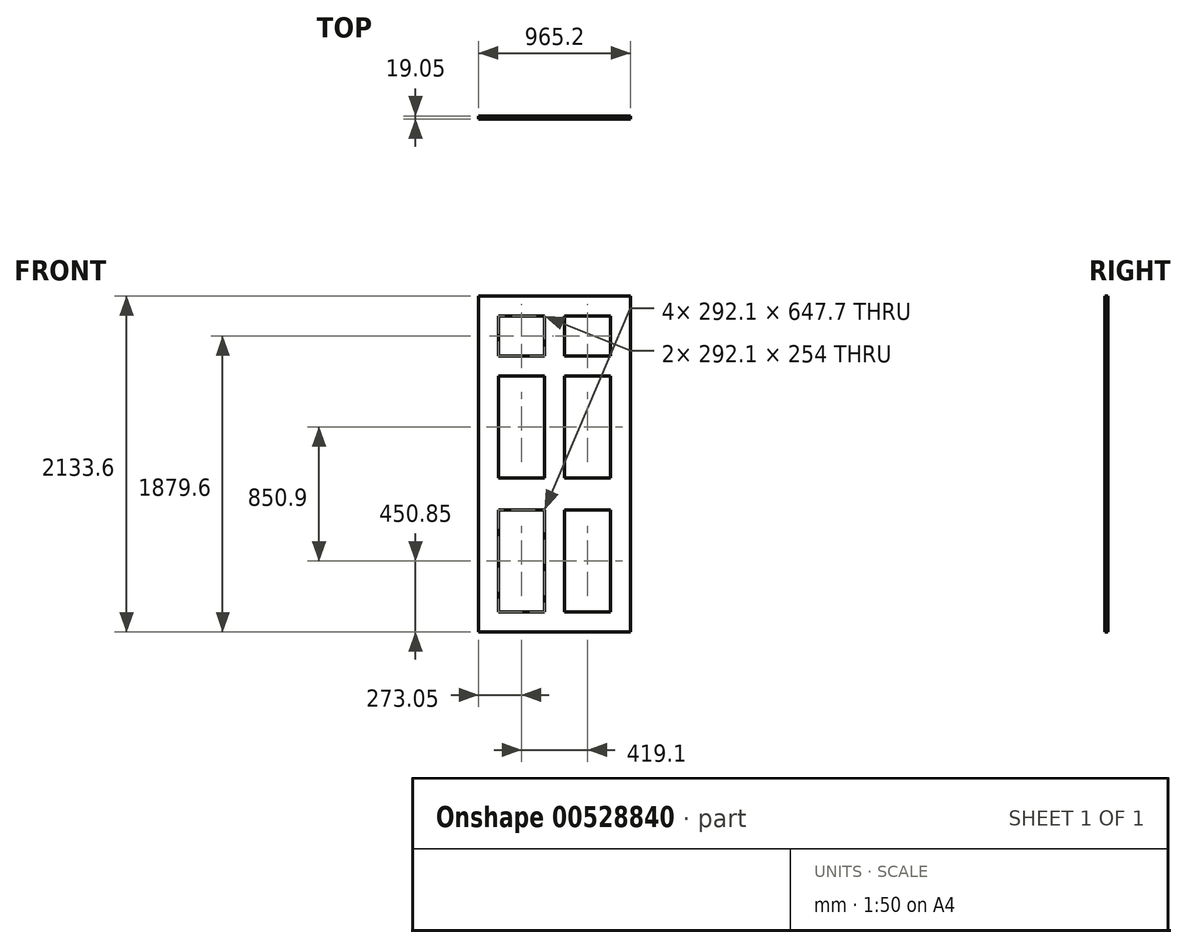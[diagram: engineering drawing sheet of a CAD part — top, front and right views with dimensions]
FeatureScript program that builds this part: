
annotation { "Feature Type Name" : "Feature", "Feature Type Description" : "" }
export const myFeature = defineFeature(function(context is Context, id is Id, definition is map)
    precondition{}
    {
        {
            var Q0;
            Q0=qCreatedBy(makeId("Front.planeOp"),FACE);
            var sketch = newSketch(context, id + "F0", { "sketchPlane" : qUnion([Q0])});
            skLineSegment(sketch, "E0.bottom", {"start": v(482.6, -1066.8) * mm, "end": v(-482.6, -1066.8) * mm});
            skLineSegment(sketch, "E0.top", {"start": v(482.6, 1066.8) * mm, "end": v(-482.6, 1066.8) * mm});
            skLineSegment(sketch, "E0.left", {"start": v(482.6, -1066.8) * mm, "end": v(482.6, 1066.8) * mm});
            skLineSegment(sketch, "E0.right", {"start": v(-482.6, -1066.8) * mm, "end": v(-482.6, 1066.8) * mm});
            skPoint(sketch, "E0.middle", {"position": v(0, 0) * mm});
            skLineSegment(sketch, "E1", {"start": v(-355.6, 939.8) * mm, "end": v(-355.6, -88.9) * mm});
            skLineSegment(sketch, "E2", {"start": v(-355.6, 939.8) * mm, "end": v(-63.5, 939.8) * mm});
            skPoint(sketch, "E3.orphan", {"position": v(-355.6, 1066.8) * mm});
            skLineSegment(sketch, "E4", {"start": v(355.6, 939.8) * mm, "end": v(355.6, 685.8) * mm});
            skPoint(sketch, "E5.orphan", {"position": v(482.6, 939.8) * mm});
            skLineSegment(sketch, "E6", {"start": v(-355.6, -939.8) * mm, "end": v(-63.5, -939.8) * mm});
            skPoint(sketch, "E7.orphan", {"position": v(-355.6, -1066.8) * mm});
            skPoint(sketch, "E8.orphan", {"position": v(355.6, -1066.8) * mm});
            skPoint(sketch, "E9.orphan", {"position": v(-482.6, -939.8) * mm});
            skLineSegment(sketch, "E10", {"start": v(-63.5, 939.8) * mm, "end": v(-63.5, 685.8) * mm});
            skLineSegment(sketch, "E11", {"start": v(63.5, -939.8) * mm, "end": v(63.5, -292.1) * mm});
            skLineSegment(sketch, "E12", {"start": v(-355.6, 685.8) * mm, "end": v(-63.5, 685.8) * mm});
            skLineSegment(sketch, "E13.trimOffspring", {"start": v(63.5, 939.8) * mm, "end": v(355.6, 939.8) * mm});
            skLineSegment(sketch, "E14.trimOffspring", {"start": v(63.5, 685.8) * mm, "end": v(355.6, 685.8) * mm});
            skLineSegment(sketch, "E15", {"start": v(-355.6, 558.8) * mm, "end": v(-63.5, 558.8) * mm});
            skLineSegment(sketch, "E16.trimOffspring", {"start": v(-63.5, 558.8) * mm, "end": v(-63.5, -88.9) * mm});
            skLineSegment(sketch, "E17.trimOffspring", {"start": v(63.5, 685.8) * mm, "end": v(63.5, 939.8) * mm});
            skLineSegment(sketch, "E18.trimOffspring", {"start": v(355.6, 558.8) * mm, "end": v(355.6, -88.9) * mm});
            skLineSegment(sketch, "E19.trimOffspring", {"start": v(63.5, 558.8) * mm, "end": v(355.6, 558.8) * mm});
            skLineSegment(sketch, "E20", {"start": v(-355.6, -88.9) * mm, "end": v(-63.5, -88.9) * mm});
            skLineSegment(sketch, "E21", {"start": v(-355.6, -292.1) * mm, "end": v(-63.5, -292.1) * mm});
            skLineSegment(sketch, "E22.trimOffspring", {"start": v(-63.5, -292.1) * mm, "end": v(-63.5, -939.8) * mm});
            skLineSegment(sketch, "E23.trimOffspring", {"start": v(63.5, -88.9) * mm, "end": v(355.6, -88.9) * mm});
            skLineSegment(sketch, "E24.trimOffspring", {"start": v(355.6, -292.1) * mm, "end": v(355.6, -939.8) * mm});
            skLineSegment(sketch, "E25.trimOffspring", {"start": v(63.5, -88.9) * mm, "end": v(63.5, 558.8) * mm});
            skLineSegment(sketch, "E26.trimOffspring", {"start": v(-355.6, -292.1) * mm, "end": v(-355.6, -939.8) * mm});
            skLineSegment(sketch, "E27.trimOffspring", {"start": v(63.5, -292.1) * mm, "end": v(355.6, -292.1) * mm});
            skLineSegment(sketch, "E28.trimOffspring", {"start": v(63.5, -939.8) * mm, "end": v(355.6, -939.8) * mm});
            skSolve(sketch);
        }
        {
            var Q0;
            Q0=qSketchRegion(id+"F0",true);
            extrude(context, id + "F1", {"entities" : qUnion([Q0]), "depth" : 19.05 * mm, "offsetDistance" : 25.4 * mm});
        }
    });
